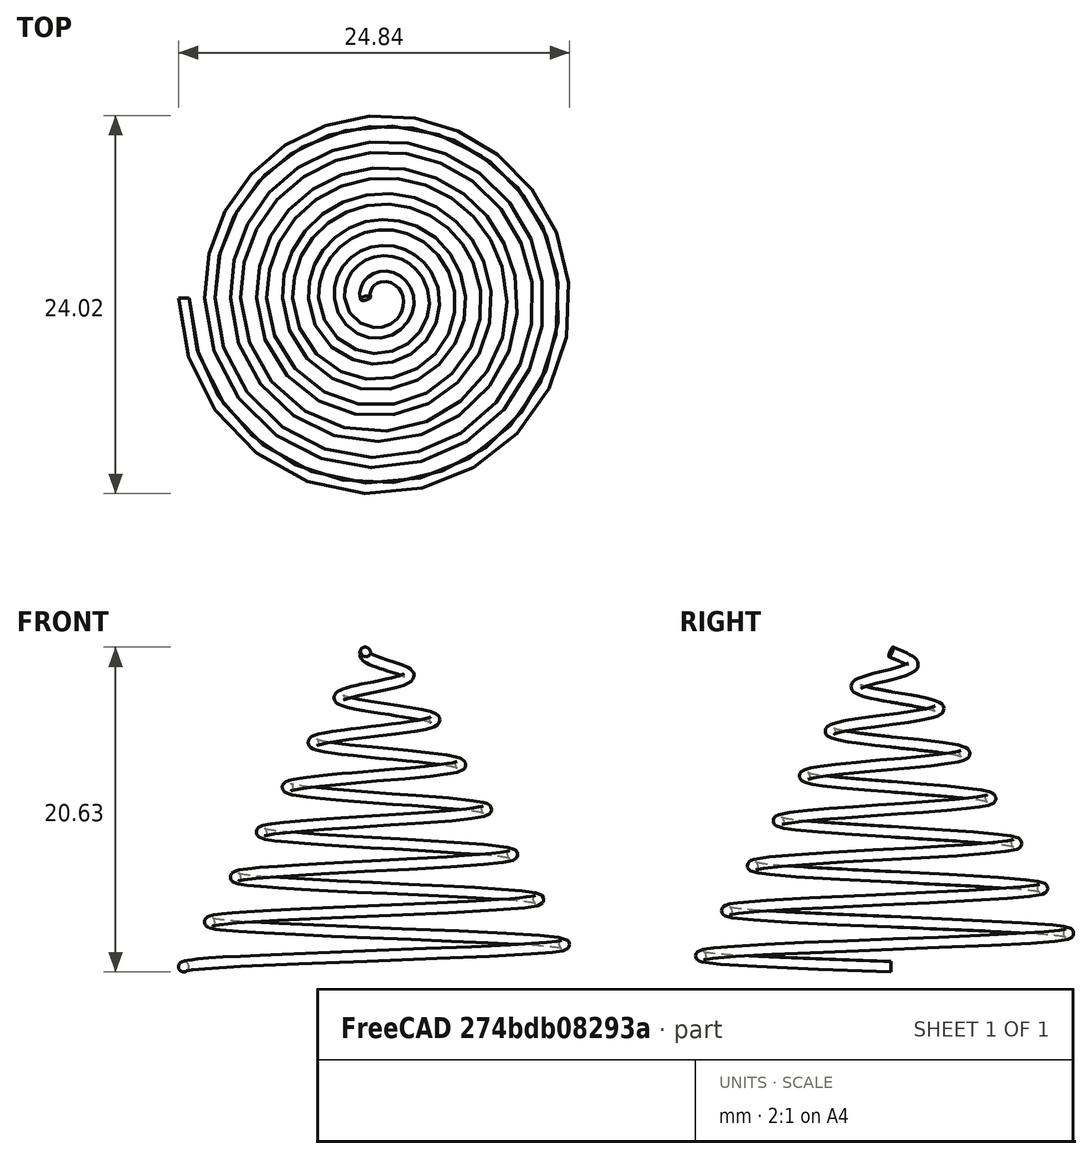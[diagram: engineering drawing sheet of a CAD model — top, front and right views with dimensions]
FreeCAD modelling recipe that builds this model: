
FCSTD DOCUMENT  (FreeCAD 0.19R24291 (Git))
Label: con_spring_stl01
License: All rights reserved
LicenseURL: http://en.wikipedia.org/wiki/All_rights_reserved
objects: Spreadsheet::Sheet×1, Sketcher::SketchObject×1, PartDesign::AdditiveHelix×1, PartDesign::Body×1
note: 4 computed .brp shape members not serialized (recipe doc carries the construction recipe); baked Part::Feature solids carry a one-line shape summary decoded from their .brp

FEATURE [Spreadsheet::Sheet] Spreadsheet
  cells = A2=con; B2=spring; C3=ring; B4=top; C4(rg_tp)=2.5; B5=botttom; C5(rg_btm)=12.5; B6=wire; C6(wire)=0.33; B7=height; C7(hgt)=20; B8=turns; C8(trn)=7
FEATURE [Sketcher::SketchObject] Sketch
  FullyConstrained = true
  MapMode = 5
  Placement = pos=(0,0,0) rot=(1,0,0;1.5708rad)
  Support = -> [XZ_Plane]
  expr: Constraints[2] = Spreadsheet.rg_btm
  expr: Constraints[1] = Spreadsheet.wire
  sketch-geometry (1):
    g0: Circle CenterX=-12.5 CenterY=0 CenterZ=0 NormalX=0 NormalY=0 NormalZ=1 AngleXU=0 Radius=0.33
  constraints (3):
    c: PointOnObject(g0,g-1)
    c: Radius(g0) = 0.33
    c: Distance(g0,g-1) = 12.5
FEATURE [PartDesign::AdditiveHelix] AdditiveHelix
  Angle = -30
  Axis = (0,-2e-16,1)
  Base = (0,0,0)
  HasBeenEdited = true
  Height = 20
  LeftHanded = false
  Mode = 2
  Outside = false
  Pitch = 2.85714
  Placement = pos=(0,0,0) rot=(1,0,0;1.5708rad)
  Profile = -> Sketch
  ReferenceAxis = -> Sketch [V_Axis]
  Turns = 7
  expr: Turns = Spreadsheet.trn
  expr: Height = Spreadsheet.hgt
FEATURE [PartDesign::Body] Body
  Group = -> [Sketch,AdditiveHelix]
  Origin = -> Origin
  Tip = -> AdditiveHelix
